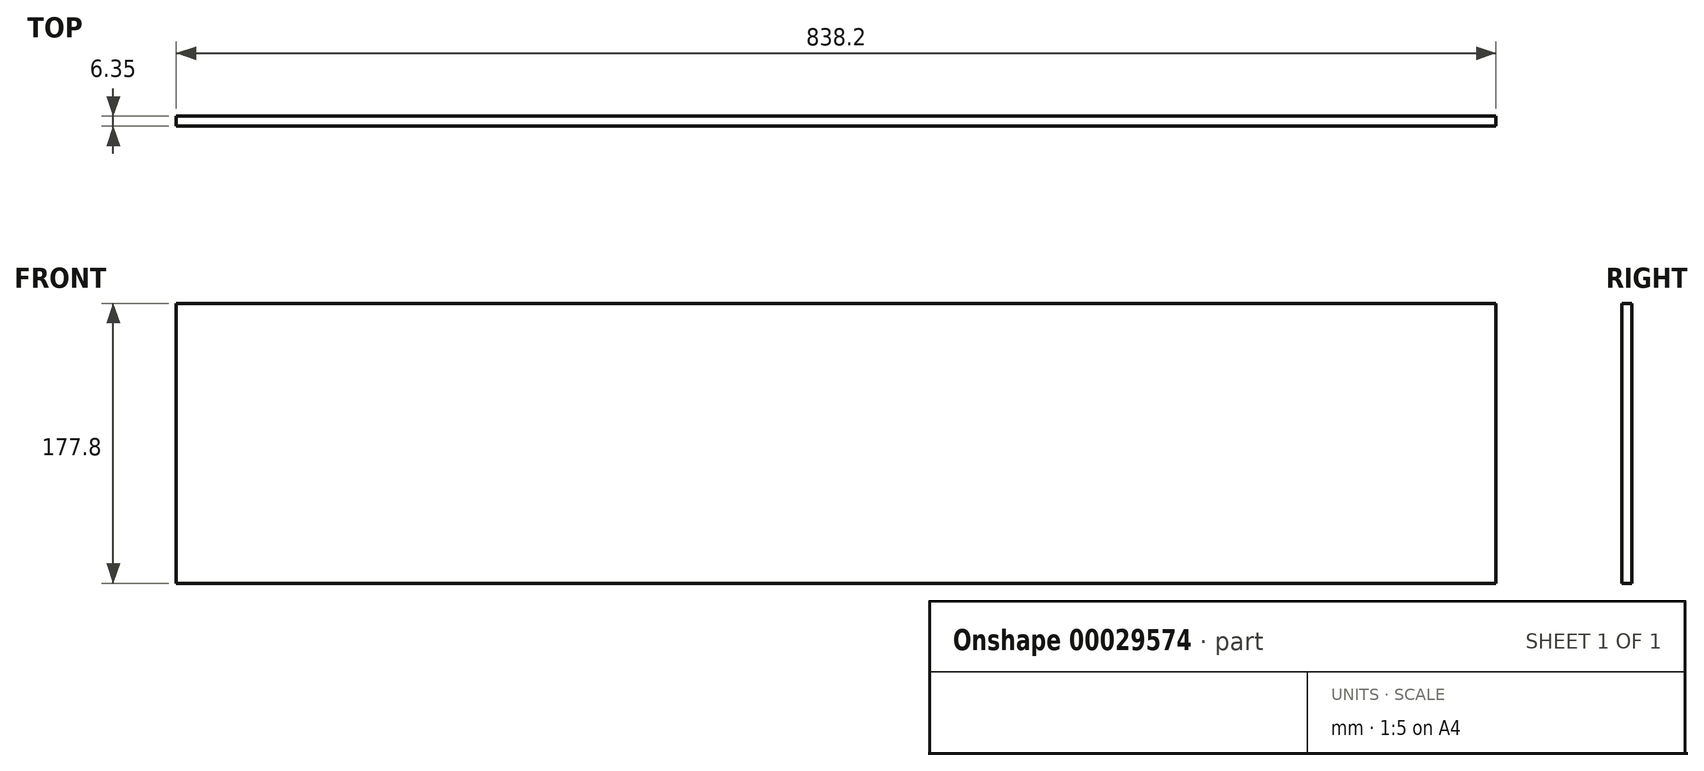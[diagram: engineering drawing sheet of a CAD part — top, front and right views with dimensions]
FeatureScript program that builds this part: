
annotation { "Feature Type Name" : "Feature", "Feature Type Description" : "" }
export const myFeature = defineFeature(function(context is Context, id is Id, definition is map)
    precondition{}
    {
        {
            var Q0;
            Q0=qCreatedBy(makeId("Front.planeOp"),FACE);
            var sketch = newSketch(context, id + "F0", { "sketchPlane" : qUnion([Q0])});
            skLineSegment(sketch, "E0.rect.bottom", {"start": v(-419.1, 88.9) * mm, "end": v(419.1, 88.9) * mm});
            skLineSegment(sketch, "E0.rect.top", {"start": v(-419.1, -88.9) * mm, "end": v(419.1, -88.9) * mm});
            skLineSegment(sketch, "E0.rect.left", {"start": v(-419.1, 88.9) * mm, "end": v(-419.1, -88.9) * mm});
            skLineSegment(sketch, "E0.rect.right", {"start": v(419.1, 88.9) * mm, "end": v(419.1, -88.9) * mm});
            skPoint(sketch, "E0.rect.middle", {"position": v(0, 0) * mm});
            skSolve(sketch);
        }
        {
            var Q0;
            Q0=makeQuery(id+"F0.imprint","IMPRINT",FACE,{"disambiguationData":[TD([[makeQuery(id+"F0.imprint","IMPRINT",EDGE,{"derivedFrom":sQuery(id+"F0.wireOp",EDGE,"E0.rect.bottom")}),-1.0]])]});
            extrude(context, id + "F1", {"entities" : qUnion([Q0]), "depth" : 6.35 * mm});
        }
    });
